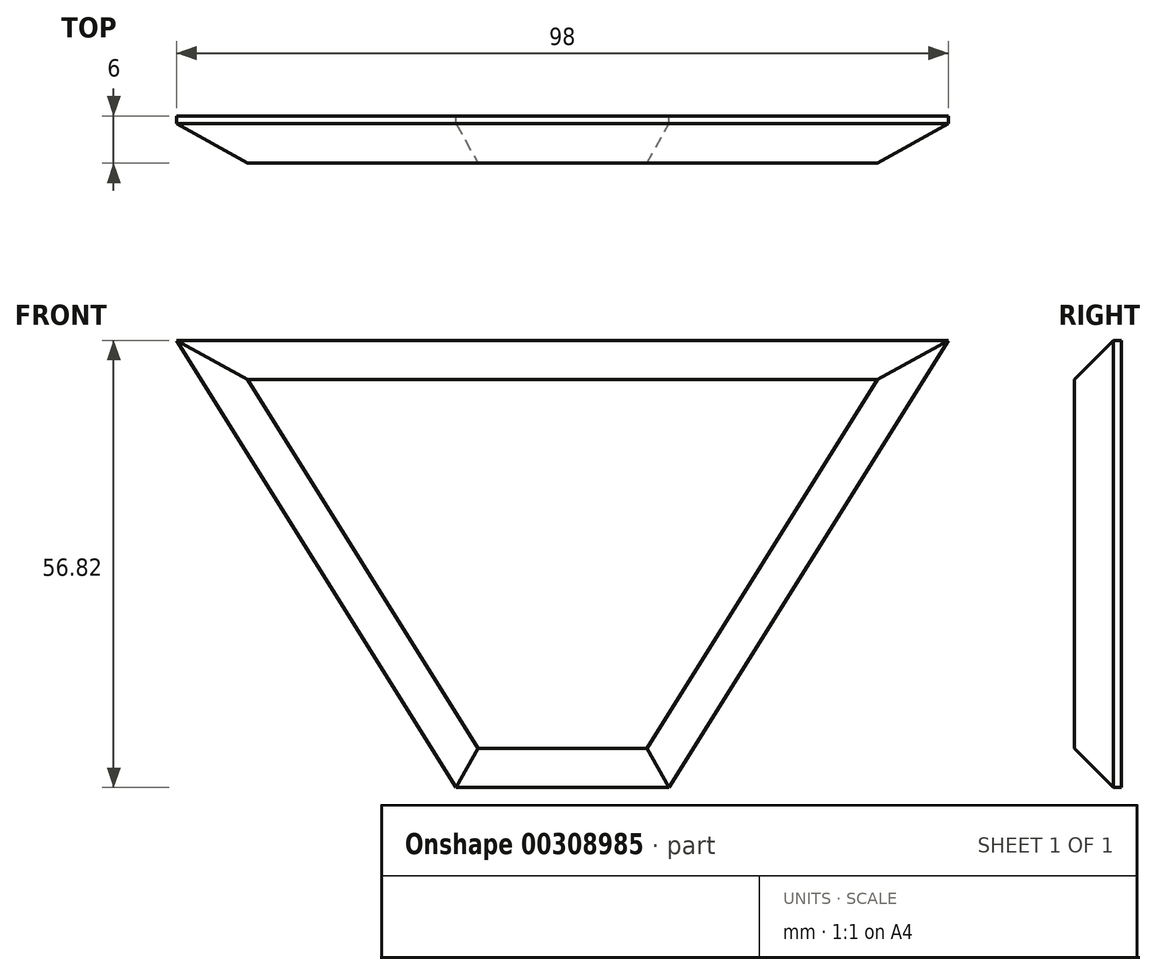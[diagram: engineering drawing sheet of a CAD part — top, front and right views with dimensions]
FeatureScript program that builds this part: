
annotation { "Feature Type Name" : "Feature", "Feature Type Description" : "" }
export const myFeature = defineFeature(function(context is Context, id is Id, definition is map)
    precondition{}
    {
        {
            var Q0;
            Q0=qCreatedBy(makeId("Front.planeOp"),FACE);
            var sketch = newSketch(context, id + "F0", { "sketchPlane" : qUnion([Q0])});
            skLineSegment(sketch, "E0", {"start": v(-49, 56.82) * mm, "end": v(-13.5, 0) * mm});
            skLineSegment(sketch, "E1", {"start": v(-13.5, 0) * mm, "end": v(13.5, 0) * mm});
            skLineSegment(sketch, "E2", {"start": v(13.5, 0) * mm, "end": v(49, 56.82) * mm});
            skLineSegment(sketch, "E3", {"start": v(49, 56.82) * mm, "end": v(-49, 56.82) * mm});
            skSolve(sketch);
        }
        {
            var Q0;
            Q0=makeQuery(id+"F0.imprint","IMPRINT",FACE,{"disambiguationData":[TD([[makeQuery(id+"F0.imprint","IMPRINT",EDGE,{"derivedFrom":sQuery(id+"F0.wireOp",EDGE,"E0")}),1.0]])]});
            extrude(context, id + "F1", {"entities" : qUnion([Q0]), "depth" : 6 * mm});
        }
        {
            var Q0;
            Q0=makeQuery(id+"F1.opExtrude","CAP_EDGE",EDGE,{"disambiguationData":[OSD([sQuery(id+"F0.wireOp",EDGE,"E0")])],"isStart":false});
            var Q1;
            Q1=makeQuery(id+"F1.opExtrude","CAP_EDGE",EDGE,{"disambiguationData":[OSD([sQuery(id+"F0.wireOp",EDGE,"E3")])],"isStart":false});
            var Q2;
            Q2=makeQuery(id+"F1.opExtrude","CAP_EDGE",EDGE,{"disambiguationData":[OSD([sQuery(id+"F0.wireOp",EDGE,"E2")])],"isStart":false});
            var Q3;
            Q3=makeQuery(id+"F1.opExtrude","CAP_EDGE",EDGE,{"disambiguationData":[OSD([sQuery(id+"F0.wireOp",EDGE,"E1")])],"isStart":false});
            chamfer(context, id + "F2", {"entities" : qUnion([Q0, Q1, Q2, Q3]), "width" : 5 * mm, "tangentPropagation" : true});
        }
    });
